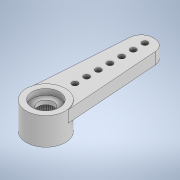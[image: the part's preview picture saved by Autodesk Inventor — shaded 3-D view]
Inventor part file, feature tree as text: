
AUTODESK INVENTOR PART (.ipt)
format: ipt  version: 2020 (Build 240168000, 168)  size: 384,000 bytes
history: native  units: mm
features: sketch x5, extrude x4, other x3, projected_geometry x2, fillet x1, hole x1
ambient origin geometry x8: Origin, YZ Plane, XZ Plane, XY Plane, X Axis, Y Axis, Z Axis, Center Point
bodies: Body1 (feature_tree)
feature tree (16):
  other  "Серво-насадка односторонняя"
  other  "Твердое тело1"
  extrude  "Выдавливание1"  Depth=6.7mm
  other  "РабПлоскость1"
  extrude  "Выдавливание2"  Depth=4.7mm TaperAngle=0.0deg
  extrude  "Выдавливание3"  [1 undecoded]
  fillet  "Сопряжение1"  Radius=18.5mm
  hole  "Отверстие1"  [1 undecoded]
  extrude  "Выдавливание5"  Depth=2.0mm TaperAngle=0.0deg
  sketch  "Эскиз1"
  sketch  "Эскиз2"
  projected_geometry  "Спроецированная петля1"
  sketch  "Эскиз3"
  sketch  "Эскиз5"
  sketch  "Эскиз6"
  projected_geometry  "Спроецированная петля2"
note: 2 required parameter values undecoded (feature->parameter linkage not recoverable at this tier; creation-order binding heuristic only, values carry confidence <= 0.55)
